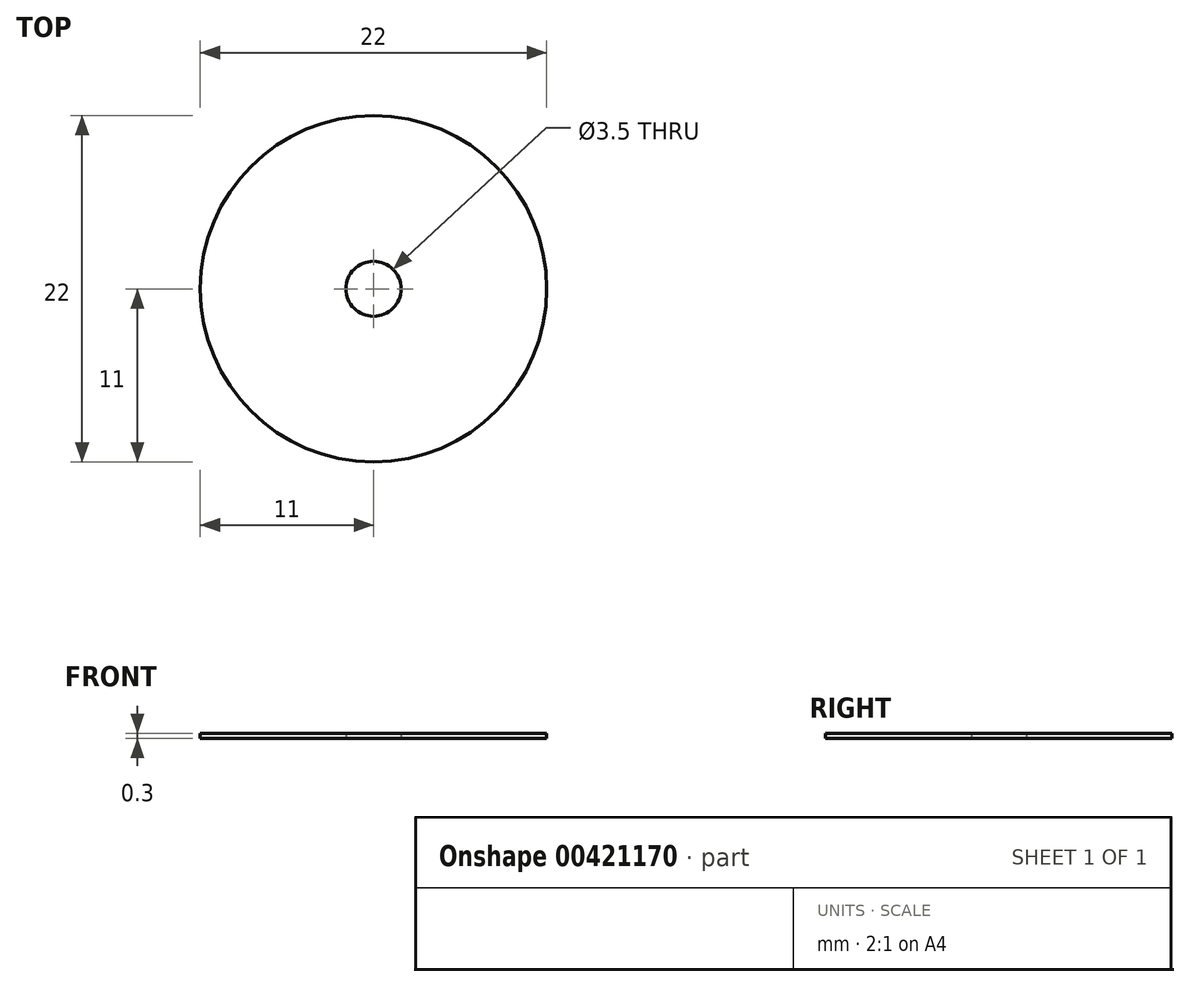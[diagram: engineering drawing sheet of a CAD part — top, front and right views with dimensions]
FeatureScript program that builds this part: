
annotation { "Feature Type Name" : "Feature", "Feature Type Description" : "" }
export const myFeature = defineFeature(function(context is Context, id is Id, definition is map)
    precondition{}
    {
        {
            var Q0;
            Q0=qCreatedBy(makeId("Top.planeOp"),FACE);
            var sketch = newSketch(context, id + "F0", { "sketchPlane" : qUnion([Q0])});
            skCircle(sketch, "E0", {"center": v(0, 0) * mm, "radius": 11 * mm});
            skCircle(sketch, "E1", {"center": v(0, 0) * mm, "radius": 1.75 * mm});
            skSolve(sketch);
        }
        {
            var Q0;
            Q0=makeQuery(id+"F0.imprint","IMPRINT",FACE,{"disambiguationData":[TD([[makeQuery(id+"F0.imprint","IMPRINT",EDGE,{"derivedFrom":sQuery(id+"F0.wireOp",EDGE,"E0")}),1.0]])]});
            extrude(context, id + "F1", {"entities" : qUnion([Q0]), "endBound" : BoundingType.SYMMETRIC, "depth" : .3 * mm});
        }
    });
